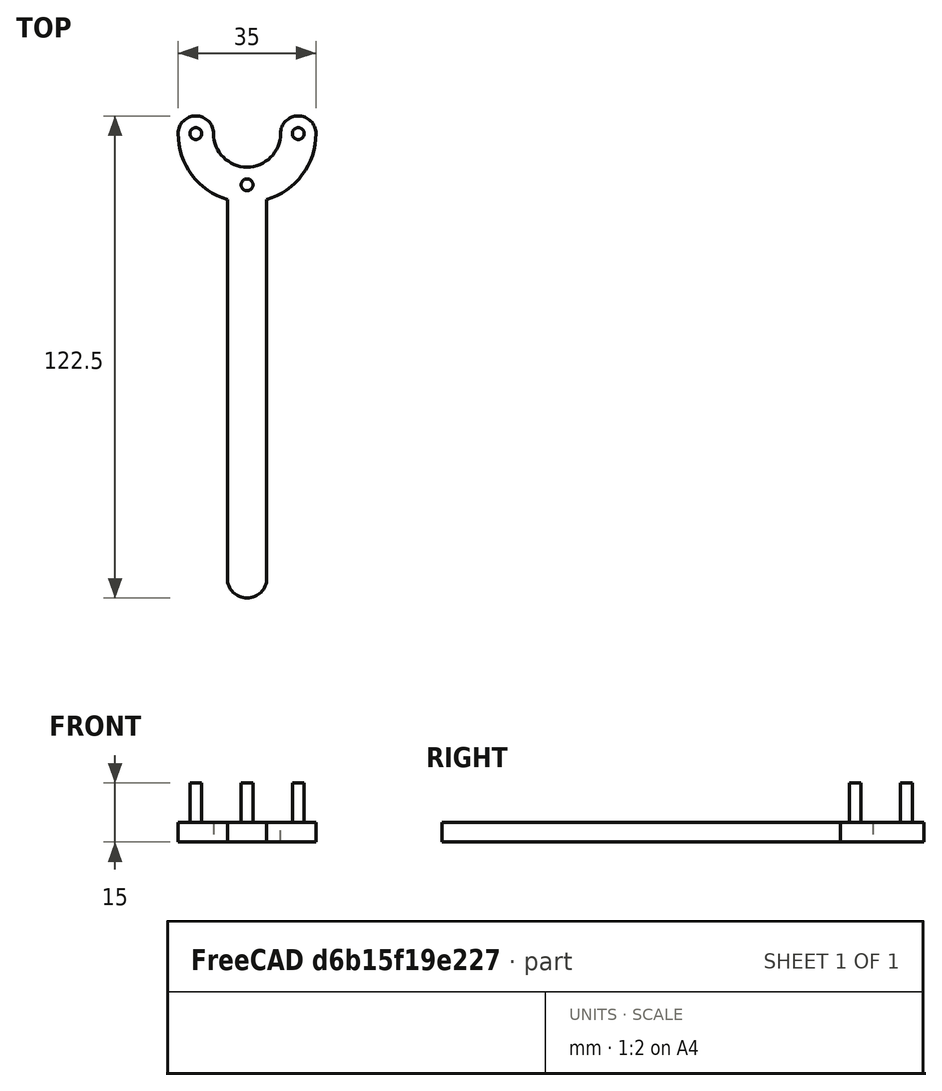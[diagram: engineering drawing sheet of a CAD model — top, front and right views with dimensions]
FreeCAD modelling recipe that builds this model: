
FCSTD DOCUMENT  (FreeCAD 0.20R)
Label: XL30WehneltWrench
License: All rights reserved
LicenseURL: http://en.wikipedia.org/wiki/All_rights_reserved
objects: TechDraw::DrawViewDimension×13, Part::Cylinder×8, TechDraw::DrawProjGroupItem×4, Part::Box×2, Part::Cut×2, Part::MultiFuse×2, Spreadsheet::Sheet×1, TechDraw::DrawSVGTemplate×1, TechDraw::DrawProjGroup×1, TechDraw::DrawPage×1
note: 14 computed .brp shape members not serialized (recipe doc carries the construction recipe); baked Part::Feature solids carry a one-line shape summary decoded from their .brp

FEATURE [Part::Box] Box  label="Cube"
  AttacherType = Attacher::AttachEngine3D
  Height = 5
  Length = 35
  Placement = pos=(-17.5,0,0) rot=(0,0,1;0rad)
  Width = 30.5
  expr: .Placement.Base.x = -(<<WrenchParameters>>.diameter_pinring + <<WrenchParameters>>.width_material) / 2
  expr: Height = <<WrenchParameters>>.thickness
  expr: Length = <<WrenchParameters>>.diameter_pinring + <<WrenchParameters>>.width_material
  expr: Width = <<WrenchParameters>>.diameter_pinring + <<WrenchParameters>>.width_material / 2
FEATURE [Part::Box] Box001  label="Cube001"
  AttacherType = Attacher::AttachEngine3D
  Height = 5
  Length = 10
  Placement = pos=(-5,-113,0) rot=(0,0,1;0rad)
  Width = 100
  expr: .Placement.Base.x = -<<WrenchParameters>>.width_handle / 2
  expr: .Placement.Base.y = -<<WrenchParameters>>.length_handle - <<WrenchParameters>>.diameter_pinring / 2
  expr: Height = <<WrenchParameters>>.thickness
  expr: Length = <<WrenchParameters>>.width_handle
  expr: Width = <<WrenchParameters>>.length_handle
FEATURE [Part::Cylinder] Cylinder
  Angle = 360
  AttacherType = Attacher::AttachEngine3D
  FirstAngle = 0
  Height = 5
  Radius = 8.5
  SecondAngle = 0
  expr: Height = <<WrenchParameters>>.thickness
  expr: Radius = <<WrenchParameters>>.diameter_pinring / 2 - <<WrenchParameters>>.width_material / 2
FEATURE [Part::Cylinder] Cylinder001
  Angle = 360
  AttacherType = Attacher::AttachEngine3D
  FirstAngle = 0
  Height = 5
  Radius = 17.5
  SecondAngle = 0
  expr: Height = <<WrenchParameters>>.thickness
  expr: Radius = <<WrenchParameters>>.diameter_pinring / 2 + <<WrenchParameters>>.width_material / 2
FEATURE [Part::Cut] Cut
  Base = -> Cylinder001
  Tool = -> Cylinder
FEATURE [Part::Cut] Cut001
  Base = -> Cut
  Tool = -> Box
FEATURE [Part::Cylinder] Cylinder002
  Angle = 360
  AttacherType = Attacher::AttachEngine3D
  FirstAngle = 0
  Height = 5
  Placement = pos=(13,0,0) rot=(0,0,1;0rad)
  Radius = 4.5
  SecondAngle = 0
  expr: .Placement.Base.x = <<WrenchParameters>>.diameter_pinring / 2
  expr: Height = <<WrenchParameters>>.thickness
  expr: Radius = <<WrenchParameters>>.width_material / 2
FEATURE [Part::Cylinder] Cylinder003
  Angle = 360
  AttacherType = Attacher::AttachEngine3D
  FirstAngle = 0
  Height = 5
  Placement = pos=(-13,0,0) rot=(0,0,1;0rad)
  Radius = 4.5
  SecondAngle = 0
  expr: .Placement.Base.x = -<<WrenchParameters>>.diameter_pinring / 2
  expr: Height = <<WrenchParameters>>.thickness
  expr: Radius = <<WrenchParameters>>.width_material / 2
FEATURE [Part::Cylinder] Cylinder004
  Angle = 360
  AttacherType = Attacher::AttachEngine3D
  FirstAngle = 0
  Height = 10
  Placement = pos=(0,-13,5) rot=(0,0,1;0rad)
  Radius = 1.5
  SecondAngle = 0
  expr: .Placement.Base.y = -<<WrenchParameters>>.diameter_pinring / 2
  expr: .Placement.Base.z = <<WrenchParameters>>.thickness
  expr: Height = <<WrenchParameters>>.length_pin
  expr: Radius = <<WrenchParameters>>.diameter_pin
FEATURE [Part::Cylinder] Cylinder005
  Angle = 360
  AttacherType = Attacher::AttachEngine3D
  FirstAngle = 0
  Height = 10
  Placement = pos=(13,0,5) rot=(0,0,1;0rad)
  Radius = 1.5
  SecondAngle = 0
  expr: .Placement.Base.x = <<WrenchParameters>>.diameter_pinring / 2
  expr: .Placement.Base.z = <<WrenchParameters>>.thickness
  expr: Height = <<WrenchParameters>>.length_pin
  expr: Radius = <<WrenchParameters>>.diameter_pin
FEATURE [Part::Cylinder] Cylinder006
  Angle = 360
  AttacherType = Attacher::AttachEngine3D
  FirstAngle = 0
  Height = 10
  Placement = pos=(-13,0,5) rot=(0,0,1;0rad)
  Radius = 1.5
  SecondAngle = 0
  expr: .Placement.Base.x = -<<WrenchParameters>>.diameter_pinring / 2
  expr: .Placement.Base.z = <<WrenchParameters>>.thickness
  expr: Height = <<WrenchParameters>>.length_pin
  expr: Radius = <<WrenchParameters>>.diameter_pin
FEATURE [Part::Cylinder] Cylinder007
  Angle = 360
  AttacherType = Attacher::AttachEngine3D
  FirstAngle = 0
  Height = 5
  Placement = pos=(0,-113,0) rot=(0,0,1;0rad)
  Radius = 5
  SecondAngle = 0
  expr: .Placement.Base.y = -<<WrenchParameters>>.length_handle - <<WrenchParameters>>.diameter_pinring / 2
  expr: Height = <<WrenchParameters>>.thickness
  expr: Radius = <<WrenchParameters>>.width_handle / 2
FEATURE [Part::MultiFuse] Fusion
  Shapes = -> [Cut001,Cylinder002,Cylinder003]
FEATURE [Part::MultiFuse] Fusion001  label="XL30WehneltWrench"
  Shapes = -> [Fusion,Box001,Cylinder004,Cylinder005,Cylinder006,Cylinder007]
FEATURE [Spreadsheet::Sheet] Spreadsheet  label="WrenchParameters"
  cells = A2=Pin diameter; B2(diameter_pin)=1.5; A3=Pin ring diameter; B3(diameter_pinring)=26; A4=Material width; B4(width_material)=9; A5=Handle length; B5(length_handle)=100; A6=Handle width; B6(width_handle)=10; A7=Thickness; B7(thickness)=5; A8=Pin length; B8(length_pin)=10
FEATURE [TechDraw::DrawSVGTemplate] Template
  EditableTexts = Designed_by_Name=Thomas Spielauer; FC-Date=2023-12-01; FC-SC=mm; FC-SH=1/1; FC-Title=Wrench for Wehnelt cylinder; Subtitle=Compatible with XL30
  Height = 210
  Orientation = 1
  Width = 297
FEATURE [TechDraw::DrawProjGroupItem] ProjItem  label="Front"
  CoarseView = false
  Direction = (0,0,1)
  Focus = 100
  HardHidden = false
  IsoCount = 0
  IsoHidden = false
  IsoVisible = false
  LockPosition = true
  Perspective = false
  Rotation = 0
  RotationVector = (1,0,0)
  ScaleType = 2
  SeamHidden = false
  SeamVisible = true
  SmoothHidden = false
  SmoothVisible = true
  Source = -> [Fusion001]
  Type = 0
  X = 0
  XDirection = (1e-16,-1,0)
  Y = 0
FEATURE [TechDraw::DrawProjGroupItem] ProjItem001  label="Top"
  CoarseView = false
  Direction = (1,1e-16,0)
  Focus = 100
  HardHidden = false
  IsoCount = 0
  IsoHidden = false
  IsoVisible = false
  LockPosition = false
  Perspective = false
  Rotation = 0
  RotationVector = (1,0,0)
  ScaleType = 2
  SeamHidden = false
  SeamVisible = true
  SmoothHidden = false
  SmoothVisible = true
  Source = -> [Fusion001]
  Type = 4
  X = 0
  XDirection = (1e-16,-1,0)
  Y = -57.6225
FEATURE [TechDraw::DrawProjGroupItem] ProjItem002  label="Right"
  CoarseView = false
  Direction = (1e-16,-1,1e-16)
  Focus = 100
  HardHidden = false
  IsoCount = 0
  IsoHidden = false
  IsoVisible = false
  LockPosition = false
  Perspective = false
  Rotation = 0
  RotationVector = (1,0,0)
  ScaleType = 2
  SeamHidden = false
  SeamVisible = true
  SmoothHidden = false
  SmoothVisible = true
  Source = -> [Fusion001]
  Type = 2
  X = -102.436
  XDirection = (0,-1e-16,-1)
  Y = 0
FEATURE [TechDraw::DrawProjGroupItem] ProjItem003  label="FrontTopRight"
  CoarseView = false
  Direction = (0.57735,-0.57735,0.57735)
  Focus = 100
  HardHidden = false
  IsoCount = 0
  IsoHidden = false
  IsoVisible = false
  LockPosition = false
  Perspective = false
  Rotation = 0
  RotationVector = (1,0,0)
  ScaleType = 2
  SeamHidden = false
  SeamVisible = true
  SmoothHidden = false
  SmoothVisible = true
  Source = -> [Fusion001]
  Type = 7
  X = -113.956
  XDirection = (0,-0.707107,-0.707107)
  Y = -97.9492
FEATURE [TechDraw::DrawProjGroup] ProjGroup
  Anchor = -> ProjItem
  AutoDistribute = false
  LockPosition = false
  ProjectionType = 0
  Rotation = 0
  ScaleType = 0
  Source = -> [Fusion001]
  Views = -> [ProjItem,ProjItem001,ProjItem002,ProjItem003]
  X = 179.752
  Y = 154.165
  spacingX = 15
  spacingY = 15
FEATURE [TechDraw::DrawViewDimension] Dimension
  AngleOverride = false
  Arbitrary = false
  ArbitraryTolerances = false
  EqualTolerance = true
  ExtensionAngle = 0
  FormatSpec = %.2w
  FormatSpecOverTolerance = %+.2w
  FormatSpecUnderTolerance = %+.2w
  Inverted = false
  LineAngle = 0
  LockPosition = false
  MeasureType = 1
  OverTolerance = 0
  References2D = -> [ProjItem]
  Rotation = 0
  ScaleType = 0
  TheoreticalExact = false
  Type = 1
  UnderTolerance = 0
  X = 39.7108
  Y = 14.272
FEATURE [TechDraw::DrawViewDimension] Dimension001
  AngleOverride = false
  Arbitrary = false
  ArbitraryTolerances = false
  EqualTolerance = true
  ExtensionAngle = 0
  FormatSpec = R%.2w
  FormatSpecOverTolerance = %+.2w
  FormatSpecUnderTolerance = %+.2w
  Inverted = false
  LineAngle = 0
  LockPosition = false
  MeasureType = 1
  OverTolerance = 0
  References2D = -> [ProjItem]
  Rotation = 0
  ScaleType = 0
  TheoreticalExact = false
  Type = 4
  UnderTolerance = 0
  X = 68.2921
  Y = 21.0554
FEATURE [TechDraw::DrawViewDimension] Dimension002
  AngleOverride = false
  Arbitrary = false
  ArbitraryTolerances = false
  EqualTolerance = true
  ExtensionAngle = 0
  FormatSpec = %.2w
  FormatSpecOverTolerance = %+.2w
  FormatSpecUnderTolerance = %+.2w
  Inverted = false
  LineAngle = 0
  LockPosition = false
  MeasureType = 1
  OverTolerance = 0
  References2D = -> [ProjItem]
  Rotation = 0
  ScaleType = 0
  TheoreticalExact = false
  Type = 2
  UnderTolerance = 0
  X = 72.1488
  Y = -9.90782
FEATURE [TechDraw::DrawViewDimension] Dimension003
  AngleOverride = false
  Arbitrary = false
  ArbitraryTolerances = false
  EqualTolerance = true
  ExtensionAngle = 0
  FormatSpec = R%.2w
  FormatSpecOverTolerance = %+.2w
  FormatSpecUnderTolerance = %+.2w
  Inverted = false
  LineAngle = 0
  LockPosition = false
  MeasureType = 1
  OverTolerance = 0
  References2D = -> [ProjItem]
  Rotation = 0
  ScaleType = 0
  TheoreticalExact = false
  Type = 4
  UnderTolerance = 0
  X = -18.7139
  Y = -14.2567
FEATURE [TechDraw::DrawViewDimension] Dimension004
  AngleOverride = false
  Arbitrary = false
  ArbitraryTolerances = false
  EqualTolerance = true
  ExtensionAngle = 0
  FormatSpec = R%.2w
  FormatSpecOverTolerance = %+.2w
  FormatSpecUnderTolerance = %+.2w
  Inverted = false
  LineAngle = 0
  LockPosition = false
  MeasureType = 1
  OverTolerance = 0
  References2D = -> [ProjItem]
  Rotation = 0
  ScaleType = 0
  TheoreticalExact = false
  Type = 4
  UnderTolerance = 0
  X = -32.4854
  Y = -17.0795
FEATURE [TechDraw::DrawViewDimension] Dimension005
  AngleOverride = false
  Arbitrary = false
  ArbitraryTolerances = false
  EqualTolerance = true
  ExtensionAngle = 0
  FormatSpec = ⌀%.2w
  FormatSpecOverTolerance = %+.2w
  FormatSpecUnderTolerance = %+.2w
  Inverted = false
  LineAngle = 0
  LockPosition = false
  MeasureType = 1
  OverTolerance = 0
  References2D = -> [ProjItem]
  Rotation = 0
  ScaleType = 0
  TheoreticalExact = false
  Type = 5
  UnderTolerance = 0
  X = -72.3469
  Y = 6.07673
FEATURE [TechDraw::DrawViewDimension] Dimension006
  AngleOverride = false
  Arbitrary = false
  ArbitraryTolerances = false
  EqualTolerance = true
  ExtensionAngle = 0
  FormatSpec = ⌀%.2w
  FormatSpecOverTolerance = %+.2w
  FormatSpecUnderTolerance = %+.2w
  Inverted = false
  LineAngle = 0
  LockPosition = false
  MeasureType = 1
  OverTolerance = 0
  References2D = -> [ProjItem]
  Rotation = 0
  ScaleType = 0
  TheoreticalExact = false
  Type = 5
  UnderTolerance = 0
  X = -71.5989
  Y = 18.6558
FEATURE [TechDraw::DrawViewDimension] Dimension007
  AngleOverride = false
  Arbitrary = false
  ArbitraryTolerances = false
  EqualTolerance = true
  ExtensionAngle = 0
  FormatSpec = ⌀%.2w
  FormatSpecOverTolerance = %+.2w
  FormatSpecUnderTolerance = %+.2w
  Inverted = false
  LineAngle = 0
  LockPosition = false
  MeasureType = 1
  OverTolerance = 0
  References2D = -> [ProjItem]
  Rotation = 0
  ScaleType = 0
  TheoreticalExact = false
  Type = 5
  UnderTolerance = 0
  X = -70.7785
  Y = -7.62569
FEATURE [TechDraw::DrawViewDimension] Dimension008
  AngleOverride = false
  Arbitrary = false
  ArbitraryTolerances = false
  EqualTolerance = true
  ExtensionAngle = 0
  FormatSpec = ⌀%.2w
  FormatSpecOverTolerance = %+.2w
  FormatSpecUnderTolerance = %+.2w
  Inverted = false
  LineAngle = 0
  LockPosition = false
  MeasureType = 1
  OverTolerance = 0
  References2D = -> [ProjItem]
  Rotation = 0
  ScaleType = 0
  TheoreticalExact = false
  Type = 5
  UnderTolerance = 0
  X = -40.7421
  Y = -25.7318
FEATURE [TechDraw::DrawViewDimension] Dimension009
  AngleOverride = false
  Arbitrary = false
  ArbitraryTolerances = false
  EqualTolerance = true
  ExtensionAngle = 0
  FormatSpec = %.2w
  FormatSpecOverTolerance = %+.2w
  FormatSpecUnderTolerance = %+.2w
  Inverted = false
  LineAngle = 0
  LockPosition = false
  MeasureType = 1
  OverTolerance = 0
  References2D = -> [ProjItem001]
  Rotation = 0
  ScaleType = 0
  TheoreticalExact = false
  Type = 2
  UnderTolerance = 0
  X = 65.73
  Y = 15.1658
FEATURE [TechDraw::DrawViewDimension] Dimension010
  AngleOverride = false
  Arbitrary = false
  ArbitraryTolerances = false
  EqualTolerance = true
  ExtensionAngle = 0
  FormatSpec = %.2w
  FormatSpecOverTolerance = %+.2w
  FormatSpecUnderTolerance = %+.2w
  Inverted = false
  LineAngle = 0
  LockPosition = false
  MeasureType = 1
  OverTolerance = 0
  References2D = -> [ProjItem]
  Rotation = 0
  ScaleType = 0
  TheoreticalExact = false
  Type = 6
  UnderTolerance = 0
  X = -29.4012
  Y = 17.7564
FEATURE [TechDraw::DrawViewDimension] Dimension011
  AngleOverride = false
  Arbitrary = false
  ArbitraryTolerances = false
  EqualTolerance = true
  ExtensionAngle = 0
  FormatSpec = %.2w
  FormatSpecOverTolerance = %+.2w
  FormatSpecUnderTolerance = %+.2w
  Inverted = false
  LineAngle = 0
  LockPosition = false
  MeasureType = 1
  OverTolerance = 0
  References2D = -> [ProjItem002]
  Rotation = 0
  ScaleType = 0
  TheoreticalExact = false
  Type = 1
  UnderTolerance = 0
  X = -16.7901
  Y = -24.7303
FEATURE [TechDraw::DrawViewDimension] Dimension012
  AngleOverride = false
  Arbitrary = false
  ArbitraryTolerances = false
  EqualTolerance = true
  ExtensionAngle = 0
  FormatSpec = %.2w
  FormatSpecOverTolerance = %+.2w
  FormatSpecUnderTolerance = %+.2w
  Inverted = false
  LineAngle = 0
  LockPosition = false
  MeasureType = 1
  OverTolerance = 0
  References2D = -> [ProjItem002]
  Rotation = 0
  ScaleType = 0
  TheoreticalExact = false
  Type = 0
  UnderTolerance = 0
  X = 13.1061
  Y = 35.5375
FEATURE [TechDraw::DrawPage] Page
  KeepUpdated = true
  NextBalloonIndex = 1
  ProjectionType = 0
  Template = -> Template
  Views = -> [ProjGroup,Dimension,Dimension001,Dimension002,Dimension003,Dimension004,Dimension005,Dimension006,Dimension007,Dimension008,Dimension009,Dimension010,Dimension011,Dimension012]
